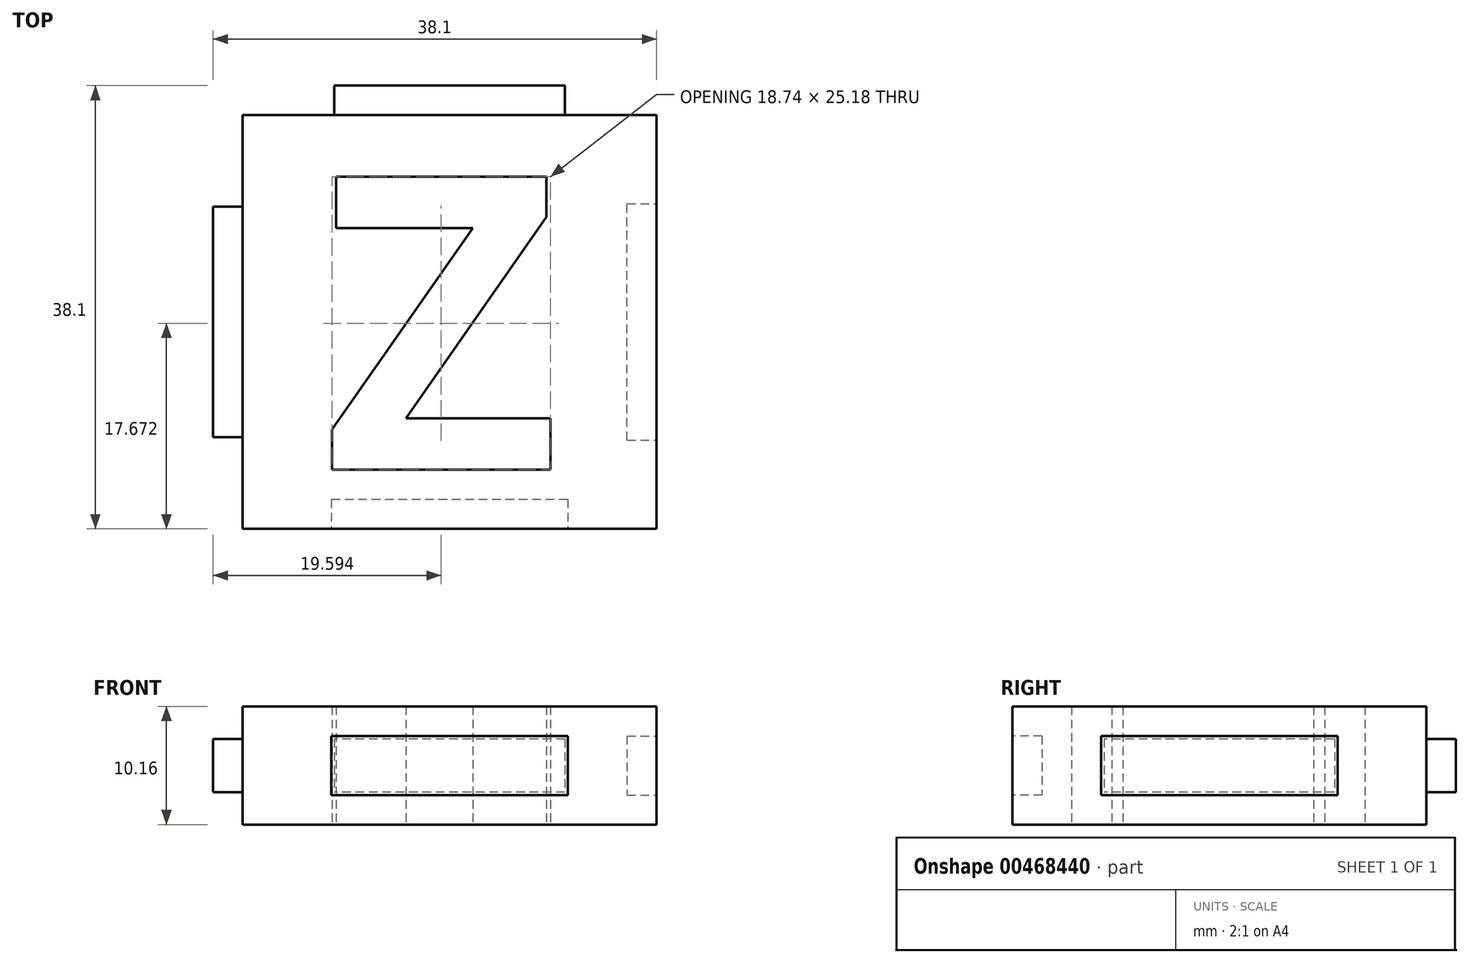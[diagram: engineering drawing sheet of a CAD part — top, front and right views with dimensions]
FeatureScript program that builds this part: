
annotation { "Feature Type Name" : "Feature", "Feature Type Description" : "" }
export const myFeature = defineFeature(function(context is Context, id is Id, definition is map)
    precondition{}
    {
        {
            var Q0;
            Q0=qCreatedBy(makeId("Top.planeOp"),FACE);
            var sketch = newSketch(context, id + "F0", { "sketchPlane" : qUnion([Q0])});
            skLineSegment(sketch, "E0.bottom", {"start": v(-17.78, 17.78) * mm, "end": v(17.78, 17.78) * mm});
            skLineSegment(sketch, "E0.top", {"start": v(-17.78, -17.78) * mm, "end": v(17.78, -17.78) * mm});
            skLineSegment(sketch, "E0.left", {"start": v(-17.78, 17.78) * mm, "end": v(-17.78, -17.78) * mm});
            skLineSegment(sketch, "E0.right", {"start": v(17.78, 17.78) * mm, "end": v(17.78, -17.78) * mm});
            skText(sketch, "E1", { "text": "Z", "fontName": "OpenSans-Bold.ttf"});
            const initialGuessF0  = {"E1": [-0.01094, -0.0127, 1, 0, 0.0254]};
            skSetInitialGuess(sketch, initialGuessF0);
            skSolve(sketch);
        }
        {
            var Q0;
            Q0=qSketchRegion(id+"F0",true);
            extrude(context, id + "F1", {"entities" : qUnion([Q0]), "endBound" : BoundingType.SYMMETRIC, "depth" : 10.16 * mm});
        }
        {
            var Q0;
            Q0=makeQuery(id+"F1.opExtrude","SWEPT_FACE",FACE,{"disambiguationData":[OSD([sQuery(id+"F0.wireOp",EDGE,"E0.bottom")])]});
            var sketch = newSketch(context, id + "F2", { "sketchPlane" : qUnion([Q0])});
            skLineSegment(sketch, "E2.bottom", {"start": v(-9.9, 2.29) * mm, "end": v(9.9, 2.29) * mm});
            skLineSegment(sketch, "E2.top", {"start": v(-9.9, -2.29) * mm, "end": v(9.9, -2.29) * mm});
            skLineSegment(sketch, "E2.left", {"start": v(-9.9, 2.29) * mm, "end": v(-9.9, -2.29) * mm});
            skLineSegment(sketch, "E2.right", {"start": v(9.9, 2.29) * mm, "end": v(9.9, -2.29) * mm});
            skSolve(sketch);
        }
        {
            var Q0;
            Q0=qSketchRegion(id+"F2",true);
            extrude(context, id + "F3", {"entities" : qUnion([Q0]), "operationType" : NewBodyOperationType.ADD, "depth" : 2.54 * mm});
        }
        {
            var Q0;
            Q0=makeQuery(id+"F1.opExtrude","SWEPT_FACE",FACE,{"disambiguationData":[OSD([sQuery(id+"F0.wireOp",EDGE,"E0.left")])]});
            var sketch = newSketch(context, id + "F4", { "sketchPlane" : qUnion([Q0])});
            skLineSegment(sketch, "E3.bottom", {"start": v(-9.9, 2.29) * mm, "end": v(9.9, 2.29) * mm});
            skLineSegment(sketch, "E3.top", {"start": v(-9.9, -2.29) * mm, "end": v(9.9, -2.29) * mm});
            skLineSegment(sketch, "E3.left", {"start": v(-9.9, 2.29) * mm, "end": v(-9.9, -2.29) * mm});
            skLineSegment(sketch, "E3.right", {"start": v(9.9, 2.29) * mm, "end": v(9.9, -2.29) * mm});
            skSolve(sketch);
        }
        {
            var Q0;
            Q0=qSketchRegion(id+"F4",true);
            extrude(context, id + "F5", {"entities" : qUnion([Q0]), "operationType" : NewBodyOperationType.ADD, "depth" : 2.54 * mm});
        }
        {
            var Q0;
            Q0=makeQuery(id+"F1.opExtrude","SWEPT_FACE",FACE,{"disambiguationData":[OSD([sQuery(id+"F0.wireOp",EDGE,"E0.top")])]});
            var sketch = newSketch(context, id + "F6", { "sketchPlane" : qUnion([Q0])});
            skLineSegment(sketch, "E4.bottom", {"start": v(-10.16, 2.54) * mm, "end": v(10.16, 2.54) * mm});
            skLineSegment(sketch, "E4.top", {"start": v(-10.16, -2.54) * mm, "end": v(10.16, -2.54) * mm});
            skLineSegment(sketch, "E4.left", {"start": v(-10.16, 2.54) * mm, "end": v(-10.16, -2.54) * mm});
            skLineSegment(sketch, "E4.right", {"start": v(10.16, 2.54) * mm, "end": v(10.16, -2.54) * mm});
            skSolve(sketch);
        }
        {
            var Q0;
            Q0=qSketchRegion(id+"F6",true);
            extrude(context, id + "F7", {"entities" : qUnion([Q0]), "operationType" : NewBodyOperationType.REMOVE, "oppositeDirection" : true, "depth" : 2.54 * mm});
        }
        {
            var Q0;
            Q0=makeQuery(id+"F1.opExtrude","SWEPT_FACE",FACE,{"disambiguationData":[OSD([sQuery(id+"F0.wireOp",EDGE,"E0.right")])]});
            var sketch = newSketch(context, id + "F8", { "sketchPlane" : qUnion([Q0])});
            skLineSegment(sketch, "E5.bottom", {"start": v(-10.16, 2.54) * mm, "end": v(10.16, 2.54) * mm});
            skLineSegment(sketch, "E5.top", {"start": v(-10.16, -2.54) * mm, "end": v(10.16, -2.54) * mm});
            skLineSegment(sketch, "E5.left", {"start": v(-10.16, 2.54) * mm, "end": v(-10.16, -2.54) * mm});
            skLineSegment(sketch, "E5.right", {"start": v(10.16, 2.54) * mm, "end": v(10.16, -2.54) * mm});
            skSolve(sketch);
        }
        {
            var Q0;
            Q0=qSketchRegion(id+"F8",true);
            extrude(context, id + "F9", {"entities" : qUnion([Q0]), "operationType" : NewBodyOperationType.REMOVE, "oppositeDirection" : true, "depth" : 2.54 * mm});
        }
    });
